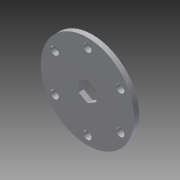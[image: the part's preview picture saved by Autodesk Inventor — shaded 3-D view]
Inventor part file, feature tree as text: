
AUTODESK INVENTOR PART (.ipt)
format: ipt  version: 2014 SP1 (Build 180222100, 222)  size: 119,296 bytes
history: native  units: in
note: dims shown in document units (in); Inventor stores cm internally (conversion verified against a paired STEP export)
features: extrude x1, sketch x1
ambient origin geometry x8: Origin, YZ Plane, XZ Plane, XY Plane, X Axis, Y Axis, Z Axis, Center Point
bodies: Solid1 (feature_tree)
feature tree (2):
  extrude  "Extrusion1"  Depth=0.125in TaperAngle=0.0deg
  sketch  "Sketch1"  dims[d0=0.5in d1=0.125in d2=0.0in]
